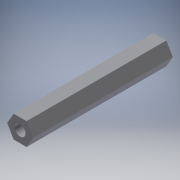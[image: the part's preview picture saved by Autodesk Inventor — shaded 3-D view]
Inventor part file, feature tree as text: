
AUTODESK INVENTOR PART (.ipt)
format: ipt  version: 2016 (Build 200138000, 138)  size: 108,032 bytes
history: native  units: in
note: dims shown in document units (in); Inventor stores cm internally (conversion verified against a paired STEP export)
features: other x1, imported_body x1, extrude x1, sketch x1
ambient origin geometry x8: Origin, YZ Plane, XZ Plane, XY Plane, X Axis, Y Axis, Z Axis, Center Point
bodies: Body1 (feature_tree)
feature tree (4):
  other  "STANDOFF_2_INCH_2011"
  imported_body  "Base1"
  extrude  "Extrusion1"  [1 undecoded]
  sketch  "Sketch1"  dims[d0=0.475in d1=0.0in]
note: 1 required parameter value undecoded (feature->parameter linkage not recoverable at this tier; creation-order binding heuristic only, values carry confidence <= 0.55)
